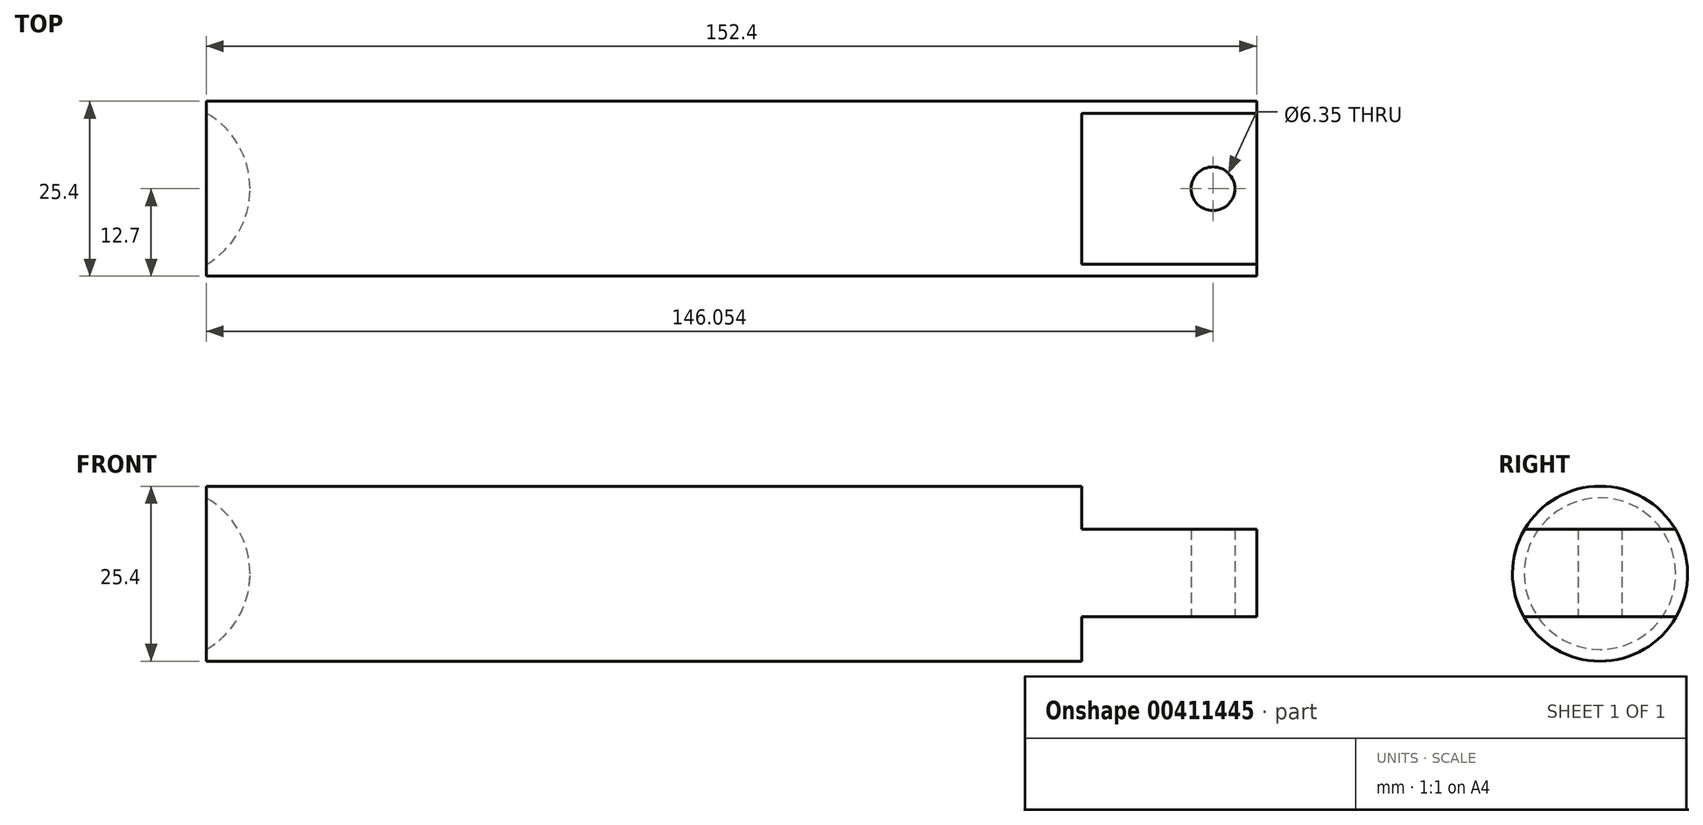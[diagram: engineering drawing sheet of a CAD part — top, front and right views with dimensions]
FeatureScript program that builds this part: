
annotation { "Feature Type Name" : "Feature", "Feature Type Description" : "" }
export const myFeature = defineFeature(function(context is Context, id is Id, definition is map)
    precondition{}
    {
        {
            var Q0;
            Q0=qCreatedBy(makeId("Front.planeOp"),FACE);
            var sketch = newSketch(context, id + "F0", { "sketchPlane" : qUnion([Q0])});
            skLineSegment(sketch, "E0", {"start": v(-44.38, 38.01) * mm, "end": v(82.62, 38.01) * mm});
            skLineSegment(sketch, "E1", {"start": v(82.62, 38.01) * mm, "end": v(82.62, 31.66) * mm});
            skLineSegment(sketch, "E2", {"start": v(82.62, 18.96) * mm, "end": v(82.62, 12.61) * mm});
            skLineSegment(sketch, "E3", {"start": v(82.62, 12.61) * mm, "end": v(-44.38, 12.61) * mm});
            skLineSegment(sketch, "E4", {"start": v(82.62, 18.96) * mm, "end": v(82.62, 31.66) * mm});
            skPoint(sketch, "E5.orphan", {"position": v(108.02, 25.31) * mm});
            skLineSegment(sketch, "E6", {"start": v(-44.38, 38.01) * mm, "end": v(-44.38, 36.31) * mm});
            skArc(sketch, "E7", {"start": v(-44.38, 14.31) * mm, "mid": v(-38.03, 25.31) * mm, "end": v(-44.38, 36.31) * mm});
            skLineSegment(sketch, "E8.trimOffspring", {"start": v(-44.38, 14.31) * mm, "end": v(-44.38, 12.61) * mm});
            skLineSegment(sketch, "E9", {"start": v(82.62, 25.31) * mm, "end": v(-50.73, 25.31) * mm});
            skSolve(sketch);
        }
        {
            var Q0;
            Q0=makeQuery(id+"F0.imprint","IMPRINT",FACE,{"disambiguationData":[TD([[makeQuery(id+"F0.imprint","IMPRINT",EDGE,{"derivedFrom":sQuery(id+"F0.wireOp",EDGE,"E0")}),-1.0]])]});
            var Q1;
            Q1=sQuery(id+"F0.wireOp",EDGE,"E9");
            revolve(context, id + "F1", {"entities" : qUnion([Q0]), "axis" : qUnion([Q1]), "revolveType" : RevolveType.FULL});
        }
        {
            var Q0;
            Q0=makeQuery(id+"F1.opRevolve","SWEPT_FACE",FACE,{"disambiguationData":[OSD([sQuery(id+"F0.wireOp",EDGE,"E1"),sQuery(id+"F0.wireOp",EDGE,"E4")])]});
            var sketch = newSketch(context, id + "F2", { "sketchPlane" : qUnion([Q0])});
            skLineSegment(sketch, "E10", {"start": v(0, 46.68) * mm, "end": v(0, 4.1) * mm});
            skLineSegment(sketch, "E11", {"start": v(0, 25.39) * mm, "end": v(-26.4, 25.39) * mm});
            skPoint(sketch, "E11.endSnap0", {"position": v(0, 25.39) * mm});
            skLineSegment(sketch, "E12", {"start": v(-10.96, 31.74) * mm, "end": v(0, 31.74) * mm});
            skLineSegment(sketch, "E13", {"start": v(0, 19.04) * mm, "end": v(-11.04, 19.04) * mm});
            skLineSegment(sketch, "E14", {"start": v(0, 31.74) * mm, "end": v(10.96, 31.74) * mm});
            skLineSegment(sketch, "E15", {"start": v(0, 19.04) * mm, "end": v(11.04, 19.04) * mm});
            skSolve(sketch);
        }
        {
            var Q0;
            {var subQ3=sQuery(id+"F2.wireOp",EDGE,"E12");Q0=makeQuery(id+"F2.imprint","IMPRINT",FACE,{"disambiguationData":[TD([[makeQuery(id+"F2.imprint","IMPRINT",EDGE,{"derivedFrom":subQ3}),-1.0]])]});}
            var Q1;
            {var subQ3=sQuery(id+"F2.wireOp",EDGE,"E13");Q1=makeQuery(id+"F2.imprint","IMPRINT",FACE,{"disambiguationData":[TD([[makeQuery(id+"F2.imprint","IMPRINT",EDGE,{"derivedFrom":subQ3}),-1.0]])]});}
            var Q2;
            {var subQ1=sQuery(id+"F2.wireOp",EDGE,"E14");Q2=makeQuery(id+"F2.imprint","IMPRINT",FACE,{"disambiguationData":[TD([[makeQuery(id+"F2.imprint","IMPRINT",EDGE,{"derivedFrom":subQ1}),-1.0]])]});}
            extrude(context, id + "F3", {"entities" : qUnion([Q0, Q1, Q2]), "operationType" : NewBodyOperationType.ADD, "depth" : 25.4 * mm});
        }
        {
            var Q0;
            Q0=makeQuery(id+"F3.opExtrude","SWEPT_FACE",FACE,{"disambiguationData":[OSD([sQuery(id+"F2.wireOp",EDGE,"E13"),sQuery(id+"F2.wireOp",EDGE,"E15")])]});
            var sketch = newSketch(context, id + "F4", { "sketchPlane" : qUnion([Q0])});
            skCircle(sketch, "E16", {"center": v(101.67, 0) * mm, "radius": 3.18 * mm});
            skSolve(sketch);
        }
        {
            var Q0;
            Q0=sQuery(id+"F4.wireOp",VERTEX,"E16.center");
            var Q1;
            Q1=makeQuery(id+"F1.opRevolve","SWEPT_BODY",BODY,{"disambiguationData":[OSD([sQuery(id+"F0.wireOp",EDGE,"E0"),sQuery(id+"F0.wireOp",EDGE,"E1"),sQuery(id+"F0.wireOp",EDGE,"E4"),sQuery(id+"F0.wireOp",EDGE,"E6"),sQuery(id+"F0.wireOp",EDGE,"E7"),sQuery(id+"F0.wireOp",EDGE,"E9")])]});
            hole(context, id + "F5", {"style" : HoleStyle.SIMPLE, "endStyle" : HoleEndStyle.THROUGH, "holeDiameter" : 6.35 * mm, "isTappedThrough" : true, "tappedDepth" : 12.7 * mm, "tapClearance" : 3, "locations" : qUnion([Q0]), "scope" : qUnion([Q1])});
        }
    });
